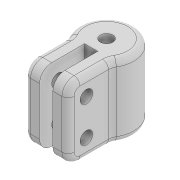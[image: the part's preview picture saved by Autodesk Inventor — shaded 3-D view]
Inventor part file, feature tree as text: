
AUTODESK INVENTOR PART (.ipt)
format: ipt  version: 2022 (Build 260153000, 153)  size: 212,480 bytes
history: native  units: mm
features: extrude x4, sketch x3, fillet x3
ambient origin geometry x8: Origin, YZ Plane, XZ Plane, XY Plane, X Axis, Y Axis, Z Axis, Center Point
bodies: Solid1 (feature_tree)
feature tree (10):
  extrude  "Extrusion1"  Depth=9.0mm
  sketch  "Sketch2"  dims[d2=12.0mm d3=0.0mm d4=2.2mm]
  extrude  "Extrusion2"  Depth=2.2mm
  extrude  "Extrusion4"  Depth=2.5mm
  extrude  "Extrusion3"  Depth=2.5mm
  fillet  "Fillet2"  Radius=10.0mm
  fillet  "Fillet3"  Radius=12.0mm
  fillet  "Fillet4"  Radius=2.1mm
  sketch  "Sketch1"  dims[d0=2.1mm d1=9.0mm]
  sketch  "Sketch3"  dims[d5=1.1mm d6=2.5mm d7=2.5mm d8=10.0mm d9=12.0mm d10=0.0mm d11=2.1mm d12=2.1mm d13=2.0mm d14=2.0mm d17=11.0mm d18=0.0mm d20=2.0mm d21=2.0mm d22=1.0mm d23=20.0mm d24=0.0mm d25=1.5mm d26=5.9mm d27=3.05mm]
